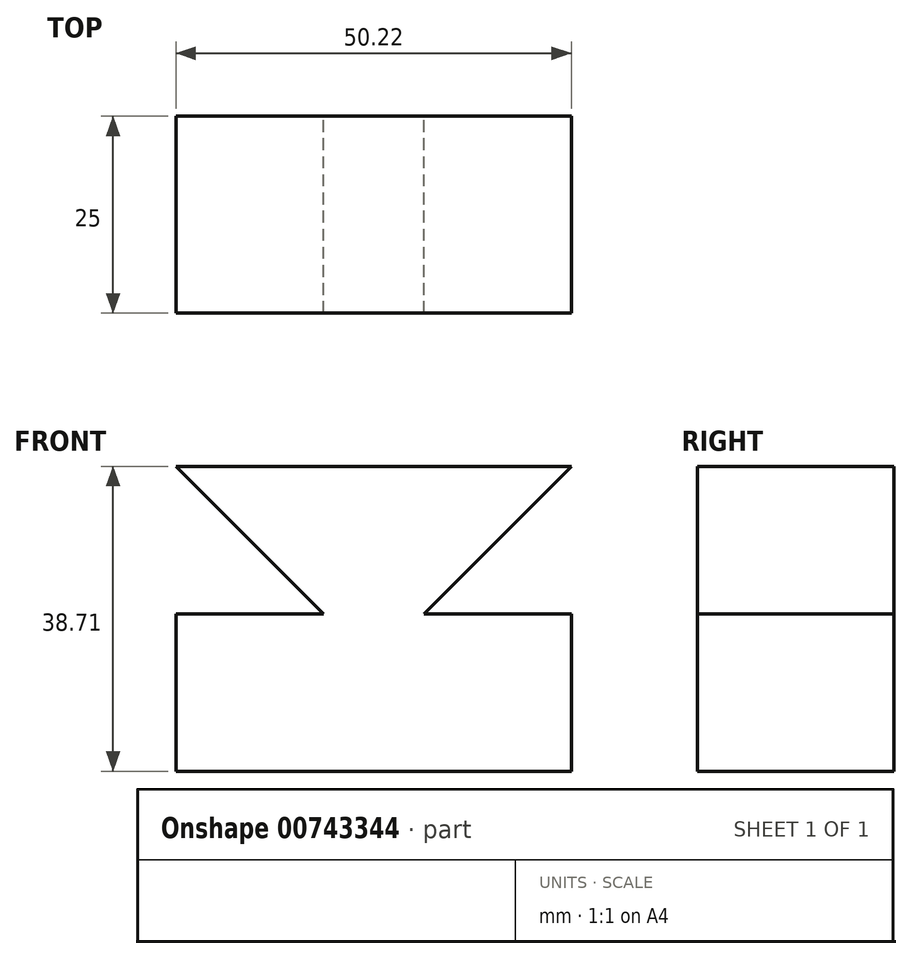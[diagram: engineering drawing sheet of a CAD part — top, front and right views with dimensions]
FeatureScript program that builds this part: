
annotation { "Feature Type Name" : "Feature", "Feature Type Description" : "" }
export const myFeature = defineFeature(function(context is Context, id is Id, definition is map)
    precondition{}
    {
        {
            var Q0;
            Q0=qCreatedBy(makeId("Front.planeOp"),FACE);
            var sketch = newSketch(context, id + "F0", { "sketchPlane" : qUnion([Q0])});
            skLineSegment(sketch, "E0", {"start": v(0, 0) * mm, "end": v(50.22, 0) * mm});
            skLineSegment(sketch, "E1", {"start": v(50.22, 0) * mm, "end": v(50.22, 19.96) * mm});
            skLineSegment(sketch, "E2", {"start": v(50.22, 19.96) * mm, "end": v(31.47, 19.96) * mm});
            skLineSegment(sketch, "E3", {"start": v(0, 0) * mm, "end": v(0, 19.96) * mm});
            skLineSegment(sketch, "E4", {"start": v(0, 19.96) * mm, "end": v(18.75, 19.96) * mm});
            skLineSegment(sketch, "E5", {"start": v(18.75, 19.96) * mm, "end": v(0, 38.7) * mm});
            skLineSegment(sketch, "E6", {"start": v(0, 38.7) * mm, "end": v(50.22, 38.7) * mm});
            skLineSegment(sketch, "E7", {"start": v(50.22, 38.7) * mm, "end": v(31.47, 19.96) * mm});
            skSolve(sketch);
        }
        {
            var Q0;
            Q0 = qSketchRegion(id + "F0", true);
            extrude(context, id + "F1", {"entities" : qUnion([Q0]), "depth" : 25 * mm, "offsetDistance" : 25 * mm});
        }
    });
